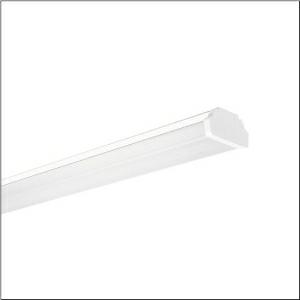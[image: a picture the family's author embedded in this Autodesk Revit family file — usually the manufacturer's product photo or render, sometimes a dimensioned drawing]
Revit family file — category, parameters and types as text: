
# Revit family: dus_r__31_ho_53bd812c1v4105_1de4
name_source: partatom
category: Lighting Fixtures
units: mm (PartAtom-declared; Revit-internal decimal feet)

## family parameters
Cut with Voids When Loaded = No
Host = Face
Light Source = No
Part Type = Normal
Room Calculation Point = No
Round Connector Dimension = Use Diameter
Shared = No

## types (1)
- --- (1 x LED, 10520 lm, 63.8 W, 4000K)
    Apparent Load = 64 VA
    CIE Flux Codes = 47 80 95 92 100
    Color Rendering = 80
    Color Temperature = 4000K
    Default Elevation = 1800 mm
    Description = DUS® 31 HO, luminaire insert, of sheet steel, coil coated, white, length: 1.535mm, width: 81mm, height: 90mm, 5x system unit, system units: 307mm, LED rated luminous flux: 10.520lm, light colour: 840, control gear: ON/OFF Multilumen, CLOi, control gear: ECG Multilumen, with plug, 3-pole, with phase selection, mains connection: 220..240V, AC, 50/60Hz, start of lifetime: 64W, end of service life: 73W, through-wiring accessed according to module size, primary optical cover: cover, of PMMA, light emission: direct distribution, primary light characteristic: symmetric, protection rating (complete): IP20, protection rating (LED compartment): IP50, insulation class (complete): insulation class I (protective earthing), certification: CE, ENEC, VDE, UKCA, impact resistance: IK03, permissible ambient temperature for indoor applications: -35..+35°C, corresponds to IFS (International Featured Standards) requirements for safety and quality in the food industry, reducing of maximum allowable ambient temperature of 5°C with ceiling mounting, packaging unit: 1 piece
    Height = 95 mm
    Lamp = 1 x LED
    Lamp Light Flux = 10520 lm
    Lamp Power = 63.8 W
    Lamp count = 1
    Length = 1535 mm
    Luminous efficacy = 165 lm/W
    Manufacturer = Siteco
    ModVariant = No
    Model = 53BD812C1V4105
    Mounting Place = Ceiling
    Mounting Type = Pendant
    Number of Poles = 1
    OnlyDefault = Yes
    Power Factor = 1
    Product Name = DUS® 31 HO
    Product group = luminaire insert
    ProductGroupID = 902
    Protection Class = Protection class I
    Protection Degree = IP 20
    RLX_Detail_Level = 1
    RLX_Emergency_Light_Flux = 0 lm
    RLX_Emergency_Type = 0
    RLX_Emergency_Type_DB = No
    RlxData = <blob elided: 39969 chars, md5=9189255c>
    Socket = socket
    Standby Power = 0 W
    System Light Flux = 10520 lm
    System Power = 64 W
    Type Comments = factory setting: luminous flux: 100 % | (A | C | E) | 144 mA
    Type Image = l_1319596.jpg
    URL = http://relux.com
    VarID = @adj_198468
    Voltage = 0 V
    Weight = 0.00 kg
    Width = 81 mm

## geometry (parser evidence)
native form markers: Blend x4, Sweep x13
no freeform markers — native parametric forms only
